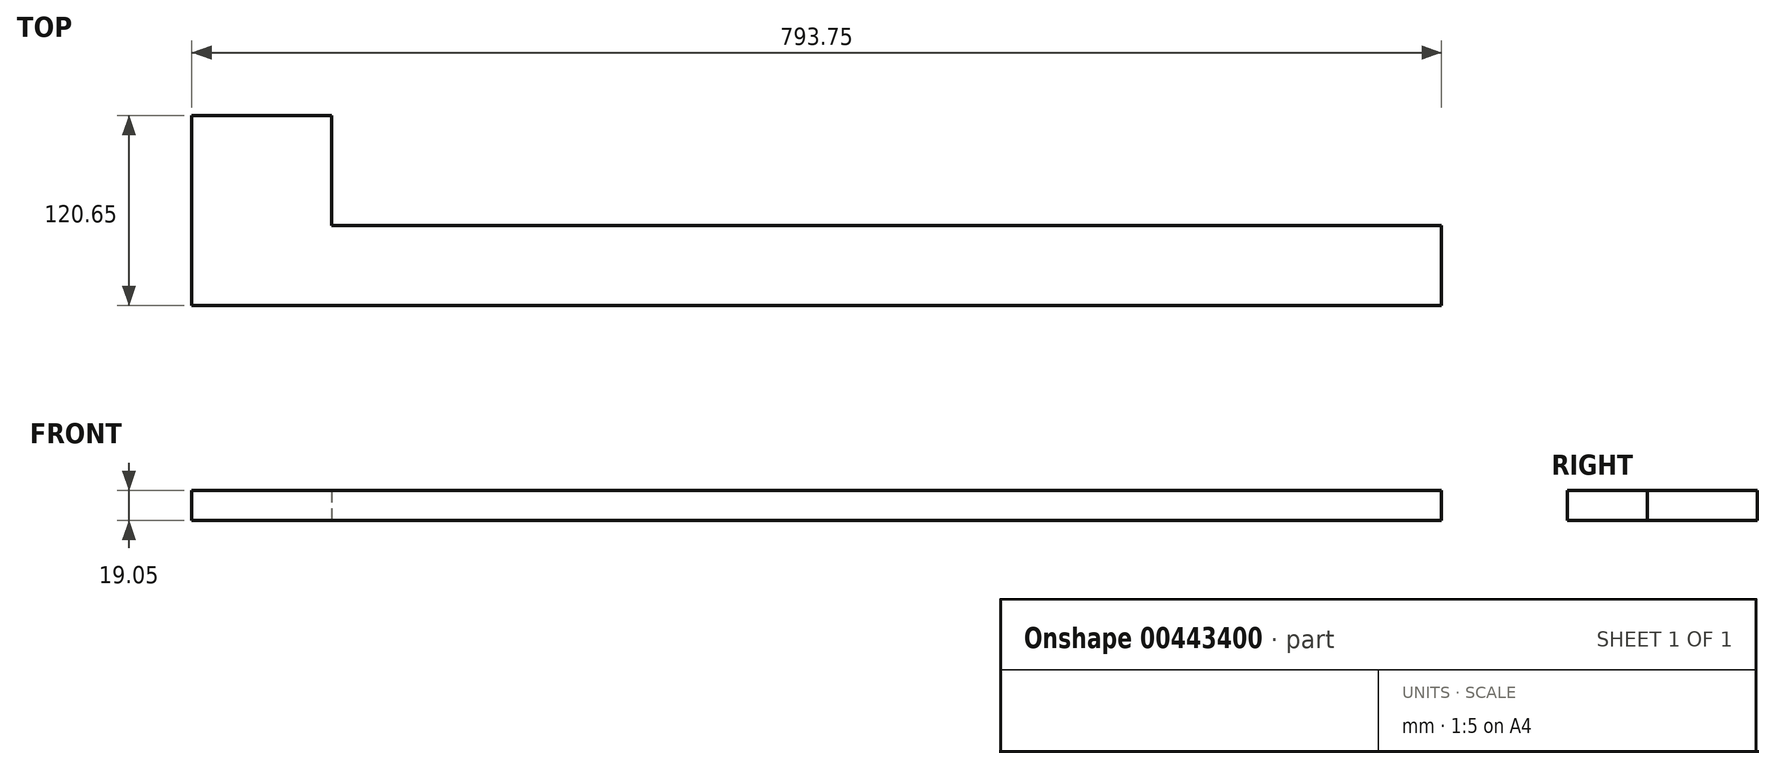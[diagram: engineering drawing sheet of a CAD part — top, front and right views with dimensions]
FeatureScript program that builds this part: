
annotation { "Feature Type Name" : "Feature", "Feature Type Description" : "" }
export const myFeature = defineFeature(function(context is Context, id is Id, definition is map)
    precondition{}
    {
        {
            var Q0;
            Q0=qCreatedBy(makeId("Top.planeOp"),FACE);
            var sketch = newSketch(context, id + "F0", { "sketchPlane" : qUnion([Q0])});
            skLineSegment(sketch, "E0", {"start": v(-310.75, 0) * mm, "end": v(483, 0) * mm});
            skLineSegment(sketch, "E1", {"start": v(483, 0) * mm, "end": v(483, 50.8) * mm});
            skLineSegment(sketch, "E2", {"start": v(483, 50.8) * mm, "end": v(-221.85, 50.8) * mm});
            skLineSegment(sketch, "E3", {"start": v(-221.85, 50.8) * mm, "end": v(-221.85, 120.65) * mm});
            skLineSegment(sketch, "E4", {"start": v(-221.85, 120.65) * mm, "end": v(-310.75, 120.65) * mm});
            skLineSegment(sketch, "E5", {"start": v(-310.75, 120.65) * mm, "end": v(-310.75, 0) * mm});
            skSolve(sketch);
        }
        {
            var Q0;
            Q0 = qSketchRegion(id + "F0", true);
            extrude(context, id + "F1", {"entities" : qUnion([Q0]), "depth" : 19.05 * mm});
        }
    });
